# Revit family: QF_COMCATER_VITAMIX50031
name_source: partatom
category: Specialty Equipment
revit_build: Autodesk Revit 2016 (Build: 20150220_1215(x64)
units: mm (PartAtom-declared; Revit-internal decimal feet)

## family parameters
Always vertical = Yes
Cut with Voids When Loaded = No
OmniClass Number = 23.40.40.14.14.11
OmniClass Title = Food Mixers
Part Type = Normal
Room Calculation Point = No
Round Connector Dimension = Use Diameter
Shared = No
Work Plane-Based = No

## types (1)
- VITAMIX50031
    Accessory = No
    Apparent Power = 1500 VA
    Assembly Code = E1090320
    Conn Conduit = No
    Cost = 0 $
    Cycle = 50 Hz
    Depth Actual = 272 mm
    Description = THE QUIET ONE BLENDING STATION ADVANCE WITH 1.4L ADVANCE CONTAINER
    Electric power = 1500 W
    FL Amps = 10 A
    Height Actual = 457 mm  [stored 1.49934 ft]
    Length Actual = 216 mm  [stored 0.708661 ft]
    Manufacturer = COMCATER ALL BRANDS
    Max Overcurrent Protection = 0 A
    Min Ckt Ampacity = 0 A
    Model = VITAMIX50031
    Number of Poles = 2
    Phase = 1
    URL = www.comcater.com.au
    Volts = 230 V
    Weight = 9.00 kg

note: [stored X ft] marks values corroborated as IEEE doubles in the binary element streams (Revit-internal decimal feet)

## geometry (parser evidence)
native form markers: Sweep x4
no freeform markers — native parametric forms only
